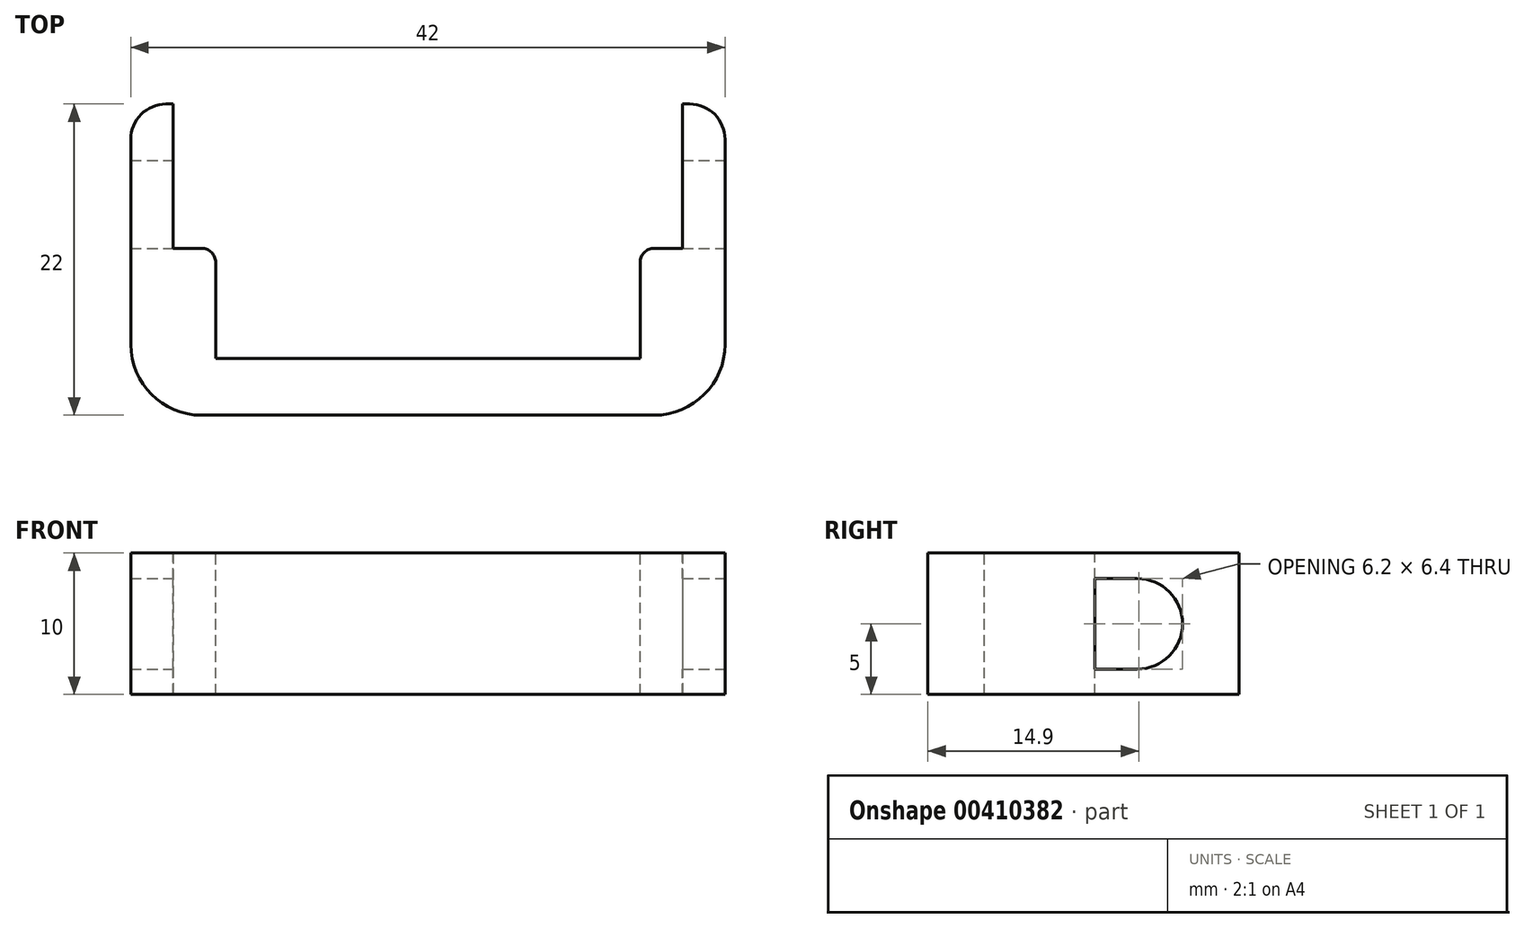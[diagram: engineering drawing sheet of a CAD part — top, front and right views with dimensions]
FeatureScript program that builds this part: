
annotation { "Feature Type Name" : "Feature", "Feature Type Description" : "" }
export const myFeature = defineFeature(function(context is Context, id is Id, definition is map)
    precondition{}
    {
        {
            var Q0;
            Q0=qCreatedBy(makeId("Top.planeOp"),FACE);
            var sketch = newSketch(context, id + "F0", { "sketchPlane" : qUnion([Q0])});
            skLineSegment(sketch, "E0", {"start": v(-21, 22) * mm, "end": v(-18, 22) * mm});
            skLineSegment(sketch, "E1", {"start": v(-18, 22) * mm, "end": v(-18, 4) * mm});
            skLineSegment(sketch, "E2", {"start": v(-18, 4) * mm, "end": v(18, 4) * mm});
            skLineSegment(sketch, "E3", {"start": v(18, 4) * mm, "end": v(18, 22) * mm});
            skLineSegment(sketch, "E4", {"start": v(18, 22) * mm, "end": v(21, 22) * mm});
            skLineSegment(sketch, "E5", {"start": v(21, 22) * mm, "end": v(21, 0) * mm});
            skLineSegment(sketch, "E6", {"start": v(21, 0) * mm, "end": v(-21, 0) * mm});
            skLineSegment(sketch, "E7", {"start": v(-21, 0) * mm, "end": v(-21, 22) * mm});
            skLineSegment(sketch, "E8", {"start": v(0, 0) * mm, "end": v(0, 4) * mm, "construction": true});
            skSolve(sketch);
        }
        {
            var Q0;
            Q0=makeQuery(id+"F0.imprint","IMPRINT",FACE,{"disambiguationData":[TD([[makeQuery(id+"F0.imprint","IMPRINT",EDGE,{"derivedFrom":sQuery(id+"F0.wireOp",EDGE,"E0")}),-1.0]])]});
            extrude(context, id + "F1", {"entities" : qUnion([Q0]), "depth" : 10 * mm, "symmetric" : true});
        }
        {
            var Q0;
            Q0=makeQuery(id+"F1.opExtrude","SWEPT_FACE",FACE,{"disambiguationData":[OSD([sQuery(id+"F0.wireOp",EDGE,"E5")])]});
            var sketch = newSketch(context, id + "F2", { "sketchPlane" : qUnion([Q0])});
            skLineSegment(sketch, "E9", {"start": v(14.8, 3.2) * mm, "end": v(11.8, 3.2) * mm});
            skLineSegment(sketch, "E10", {"start": v(11.8, 3.2) * mm, "end": v(11.8, -3.2) * mm});
            skLineSegment(sketch, "E11", {"start": v(11.8, -3.2) * mm, "end": v(14.8, -3.2) * mm});
            skArc(sketch, "E12", {"start": v(14.8, -3.2) * mm, "mid": v(18, 0) * mm, "end": v(14.8, 3.2) * mm});
            skSolve(sketch);
        }
        {
            var Q0;
            Q0=makeQuery(id+"F2.imprint","IMPRINT",FACE,{"disambiguationData":[TD([[makeQuery(id+"F2.imprint","IMPRINT",EDGE,{"derivedFrom":sQuery(id+"F2.wireOp",EDGE,"E9")}),1.0]])]});
            extrude(context, id + "F3", {"entities" : qUnion([Q0]), "operationType" : NewBodyOperationType.REMOVE, "endBound" : BoundingType.THROUGH_ALL, "oppositeDirection" : true, "depth" : 25 * mm});
        }
        {
            var Q0;
            Q0=makeQuery(id+"F1.opExtrude","CAP_FACE",FACE,{"disambiguationData":[OSD([sQuery(id+"F0.wireOp",EDGE,"E0"),sQuery(id+"F0.wireOp",EDGE,"E1"),sQuery(id+"F0.wireOp",EDGE,"E2"),sQuery(id+"F0.wireOp",EDGE,"E3"),sQuery(id+"F0.wireOp",EDGE,"E4"),sQuery(id+"F0.wireOp",EDGE,"E5"),sQuery(id+"F0.wireOp",EDGE,"E6"),sQuery(id+"F0.wireOp",EDGE,"E7")])],"isStart":false});
            var sketch = newSketch(context, id + "F4", { "sketchPlane" : qUnion([Q0])});
            skPoint(sketch, "E13.0", {"position": v(-18, 11.8) * mm});
            skPoint(sketch, "E14.0", {"position": v(18, 11.8) * mm});
            skLineSegment(sketch, "E15.bottom", {"start": v(-18, 11.8) * mm, "end": v(-15, 11.8) * mm});
            skLineSegment(sketch, "E15.top", {"start": v(-18, 4) * mm, "end": v(-15, 4) * mm});
            skLineSegment(sketch, "E15.left", {"start": v(-18, 11.8) * mm, "end": v(-18, 4) * mm});
            skLineSegment(sketch, "E15.right", {"start": v(-15, 11.8) * mm, "end": v(-15, 4) * mm});
            skLineSegment(sketch, "E16.bottom", {"start": v(18, 11.8) * mm, "end": v(15, 11.8) * mm});
            skLineSegment(sketch, "E16.top", {"start": v(18, 4) * mm, "end": v(15, 4) * mm});
            skLineSegment(sketch, "E16.left", {"start": v(18, 11.8) * mm, "end": v(18, 4) * mm});
            skLineSegment(sketch, "E16.right", {"start": v(15, 11.8) * mm, "end": v(15, 4) * mm});
            skLineSegment(sketch, "E17.0", {"start": v(-18, 4) * mm, "end": v(18, 4) * mm});
            skSolve(sketch);
        }
        {
            var Q0;
            Q0=makeQuery(id+"F4.imprint","IMPRINT",FACE,{"disambiguationData":[TD([[makeQuery(id+"F4.imprint","IMPRINT",EDGE,{"derivedFrom":sQuery(id+"F4.wireOp",EDGE,"E15.bottom")}),-1.0]])]});
            var Q1;
            Q1=makeQuery(id+"F4.imprint","IMPRINT",FACE,{"disambiguationData":[TD([[makeQuery(id+"F4.imprint","IMPRINT",EDGE,{"derivedFrom":sQuery(id+"F4.wireOp",EDGE,"E16.bottom")}),1.0]])]});
            var Q2;
            Q2=makeQuery(id+"F1.opExtrude","CAP_FACE",FACE,{"disambiguationData":[OSD([sQuery(id+"F0.wireOp",EDGE,"E0"),sQuery(id+"F0.wireOp",EDGE,"E1"),sQuery(id+"F0.wireOp",EDGE,"E2"),sQuery(id+"F0.wireOp",EDGE,"E3"),sQuery(id+"F0.wireOp",EDGE,"E4"),sQuery(id+"F0.wireOp",EDGE,"E5"),sQuery(id+"F0.wireOp",EDGE,"E6"),sQuery(id+"F0.wireOp",EDGE,"E7")])],"isStart":true});
            extrude(context, id + "F5", {"entities" : qUnion([Q0, Q1]), "operationType" : NewBodyOperationType.ADD, "endBound" : BoundingType.UP_TO_SURFACE, "oppositeDirection" : true, "endBoundEntityFace" : qUnion([Q2]), "depth" : 25 * mm});
        }
        {
            var Q0;
            Q0=makeQuery(id+"F1.opExtrude","SWEPT_EDGE",EDGE,{"disambiguationData":[OSD([sQuery(id+"F0.wireOp",EDGE,"E4"),sQuery(id+"F0.wireOp",EDGE,"E5")])]});
            var Q1;
            Q1=makeQuery(id+"F1.opExtrude","SWEPT_EDGE",EDGE,{"disambiguationData":[OSD([sQuery(id+"F0.wireOp",EDGE,"E0"),sQuery(id+"F0.wireOp",EDGE,"E7")])]});
            fillet(context, id + "F6", {"entities" : qUnion([Q0, Q1]), "radius" : 2.5 * mm, "tangentPropagation" : true, "allowEdgeOverflow" : false});
        }
        {
            var Q0;
            Q0=makeQuery(id+"F1.opExtrude","SWEPT_EDGE",EDGE,{"disambiguationData":[OSD([sQuery(id+"F0.wireOp",EDGE,"E6"),sQuery(id+"F0.wireOp",EDGE,"E7")])]});
            var Q1;
            Q1=makeQuery(id+"F1.opExtrude","SWEPT_EDGE",EDGE,{"disambiguationData":[OSD([sQuery(id+"F0.wireOp",EDGE,"E5"),sQuery(id+"F0.wireOp",EDGE,"E6")])]});
            fillet(context, id + "F7", {"entities" : qUnion([Q0, Q1]), "radius" : 5 * mm, "tangentPropagation" : true, "allowEdgeOverflow" : false});
        }
        {
            var Q0;
            Q0=makeQuery(id+"F5.opExtrude","SWEPT_EDGE",EDGE,{"disambiguationData":[OSD([sQuery(id+"F4.wireOp",EDGE,"E15.right"),sQuery(id+"F4.wireOp",EDGE,"E17.0")])]});
            var Q1;
            Q1=makeQuery(id+"F5.opExtrude","SWEPT_EDGE",EDGE,{"disambiguationData":[OSD([sQuery(id+"F4.wireOp",EDGE,"E16.right"),sQuery(id+"F4.wireOp",EDGE,"E17.0")])]});
            var Q2;
            Q2=makeQuery(id+"F5.opExtrude","SWEPT_EDGE",EDGE,{"disambiguationData":[OSD([sQuery(id+"F4.wireOp",EDGE,"E15.bottom"),sQuery(id+"F4.wireOp",EDGE,"E15.right")])]});
            var Q3;
            Q3=makeQuery(id+"F5.opExtrude","SWEPT_EDGE",EDGE,{"disambiguationData":[OSD([sQuery(id+"F4.wireOp",EDGE,"E16.bottom"),sQuery(id+"F4.wireOp",EDGE,"E16.right")])]});
            fillet(context, id + "F8", {"entities" : qUnion([Q0, Q1, Q2, Q3]), "radius" : 1 * mm, "tangentPropagation" : true, "allowEdgeOverflow" : false});
        }
    });
